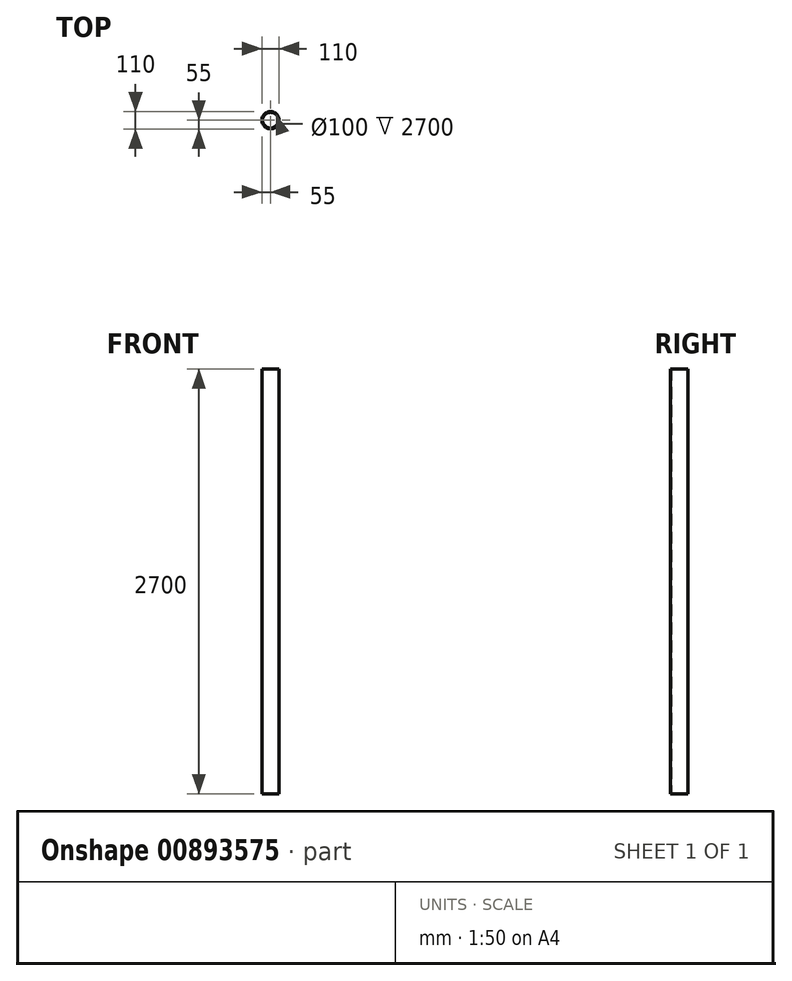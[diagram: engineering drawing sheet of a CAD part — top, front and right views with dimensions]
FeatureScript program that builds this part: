
annotation { "Feature Type Name" : "Feature", "Feature Type Description" : "" }
export const myFeature = defineFeature(function(context is Context, id is Id, definition is map)
    precondition{}
    {
        {
            var Q0;
            Q0=qCreatedBy(makeId("Top.planeOp"),FACE);
            var sketch = newSketch(context, id + "F0", { "sketchPlane" : qUnion([Q0])});
            skCircle(sketch, "E0", {"center": v(0, 0) * mm, "radius": 55 * mm});
            skCircle(sketch, "E1", {"center": v(0, 0) * mm, "radius": 50 * mm});
            skSolve(sketch);
        }
        {
            var Q0;
            Q0=makeQuery(id+"F0.imprint","IMPRINT",FACE,{"disambiguationData":[TD([[makeQuery(id+"F0.imprint","IMPRINT",EDGE,{"derivedFrom":sQuery(id+"F0.wireOp",EDGE,"E0")}),1.0]])]});
            extrude(context, id + "F1", {"entities" : qUnion([Q0]), "depth" : 2700 * mm, "offsetDistance" : 25 * mm});
        }
    });
